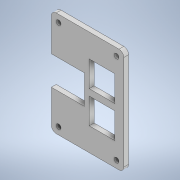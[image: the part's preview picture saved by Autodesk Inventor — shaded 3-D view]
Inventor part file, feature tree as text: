
AUTODESK INVENTOR PART (.ipt)
format: ipt  version: 2021.2 (Build 252289000, 289)  size: 123,904 bytes
history: native  units: mm
features: reference x20, other x4, extrude x1, sketch x1
ambient origin geometry x8: Origin, YZ Plane, XZ Plane, XY Plane, X Axis, Y Axis, Z Axis, Center Point
bodies: Body1 (feature_tree)
feature tree (26):
  other  "Твердое тело1"
  extrude  "Выдавливание1"  Depth=3.0mm TaperAngle=0.0deg
  sketch  "Эскиз1"
  reference  "Ссылка1"
  reference  "Ссылка2"
  reference  "Ссылка3"
  reference  "Ссылка4"
  reference  "Ссылка5"
  reference  "Ссылка6"
  reference  "Ссылка7"
  reference  "Ссылка8"
  reference  "Ссылка9"
  reference  "Ссылка10"
  reference  "Ссылка11"
  reference  "Ссылка12"
  reference  "Ссылка13"
  reference  "Ссылка14"
  reference  "Ссылка15"
  reference  "Ссылка16"
  reference  "Ссылка17"
  reference  "Ссылка18"
  reference  "Ссылка19"
  reference  "Ссылка20"
  other  "Сборка1"
  other  "level1_up:1"
  other  "plate:1"
